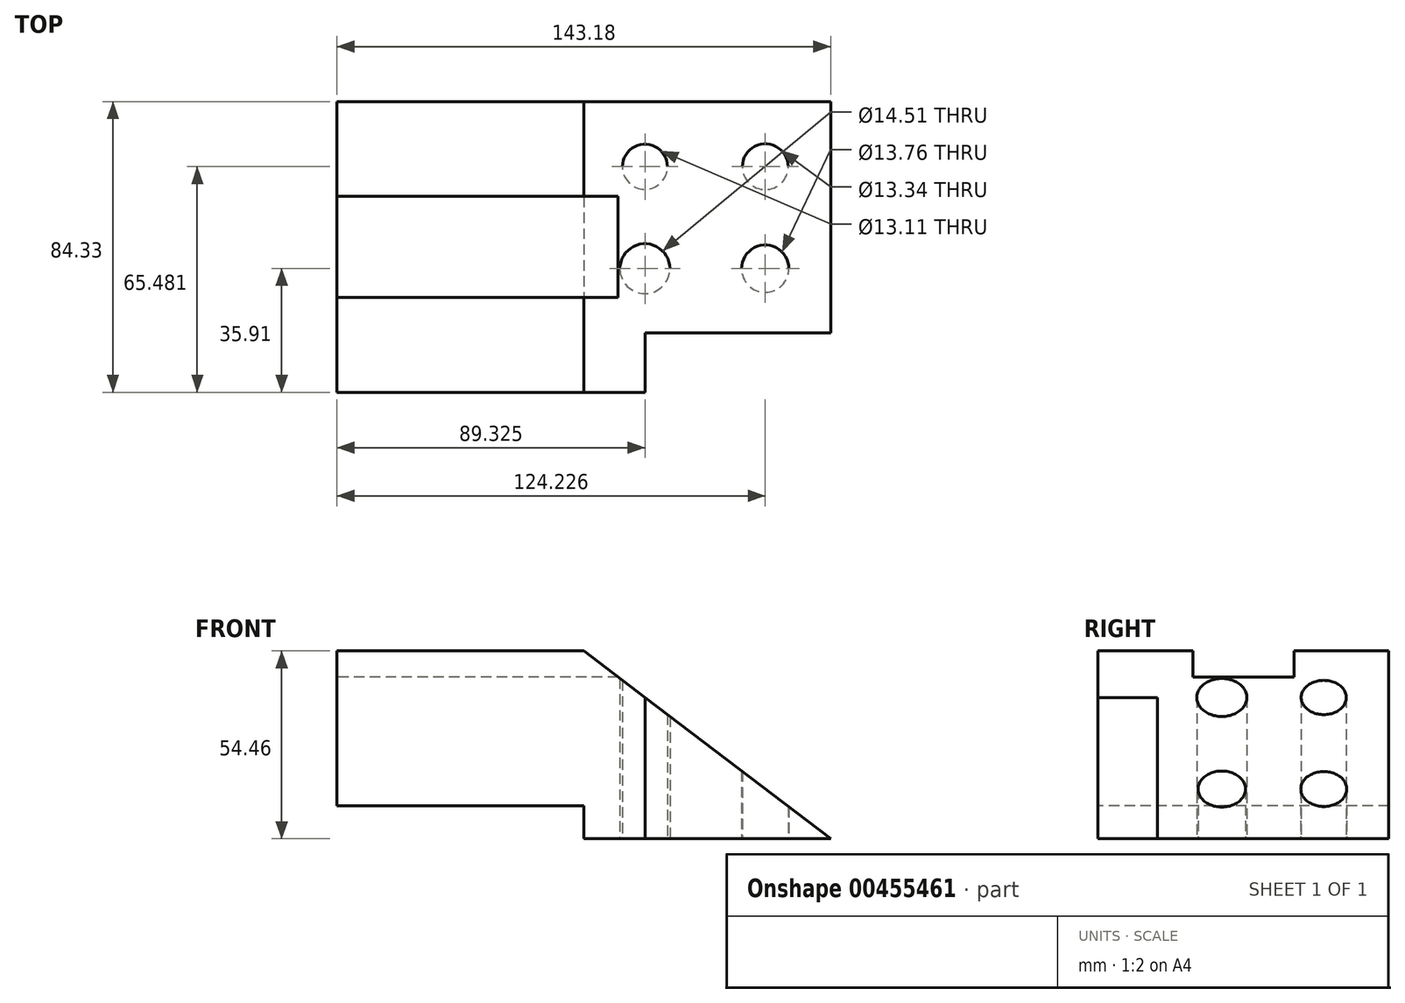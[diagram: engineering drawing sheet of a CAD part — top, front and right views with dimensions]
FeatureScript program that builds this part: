
annotation { "Feature Type Name" : "Feature", "Feature Type Description" : "" }
export const myFeature = defineFeature(function(context is Context, id is Id, definition is map)
    precondition{}
    {
        {
            var Q0;
            Q0=qCreatedBy(makeId("Front.planeOp"),FACE);
            var sketch = newSketch(context, id + "F0", { "sketchPlane" : qUnion([Q0])});
            skLineSegment(sketch, "E0.bottom", {"start": v(0, 27.23) * mm, "end": v(-71.59, 27.23) * mm});
            skLineSegment(sketch, "E0.top", {"start": v(71.59, -27.23) * mm, "end": v(-71.59, -27.23) * mm});
            skLineSegment(sketch, "E0.right", {"start": v(-71.59, 27.23) * mm, "end": v(-71.59, -27.23) * mm});
            skPoint(sketch, "E0.middle", {"position": v(0, 0) * mm});
            skLineSegment(sketch, "E1", {"start": v(0, 27.23) * mm, "end": v(71.59, -27.23) * mm});
            skSolve(sketch);
        }
        {
            var Q0;
            Q0=makeQuery(id+"F0.imprint","IMPRINT",FACE,{"disambiguationData":[TD([[makeQuery(id+"F0.imprint","IMPRINT",EDGE,{"derivedFrom":sQuery(id+"F0.wireOp",EDGE,"E0.bottom")}),1.0]])]});
            extrude(context, id + "F1", {"entities" : qUnion([Q0]), "depth" : 67.06 * mm});
        }
        {
            var Q0;
            Q0=makeQuery(id+"F1.opExtrude","CAP_FACE",FACE,{"disambiguationData":[OSD([sQuery(id+"F0.wireOp",EDGE,"E0.bottom"),sQuery(id+"F0.wireOp",EDGE,"E0.top"),sQuery(id+"F0.wireOp",EDGE,"E0.right"),sQuery(id+"F0.wireOp",EDGE,"E1")])],"isStart":false});
            var sketch = newSketch(context, id + "F2", { "sketchPlane" : qUnion([Q0])});
            skLineSegment(sketch, "E2", {"start": v(17.73, 13.74) * mm, "end": v(17.73, -27.23) * mm});
            skLineSegment(sketch, "E3", {"start": v(0, -27.23) * mm, "end": v(0, -22.04) * mm});
            skPoint(sketch, "E3.endSnap0", {"position": v(0, -27.23) * mm});
            skLineSegment(sketch, "E4", {"start": v(0, -22.04) * mm, "end": v(-71.59, -22.04) * mm});
            skSolve(sketch);
        }
        {
            var Q0;
            {var subQ0=sQuery(id+"F2.wireOp",EDGE,"E3");Q0=makeQuery(id+"F2.imprint","IMPRINT",FACE,{"disambiguationData":[TD([[makeQuery(id+"F2.imprint","IMPRINT",EDGE,{"derivedFrom":subQ0}),1.0]])]});}
            extrude(context, id + "F3", {"entities" : qUnion([Q0]), "operationType" : NewBodyOperationType.REMOVE, "oppositeDirection" : true, "depth" : 186.44 * mm});
        }
        {
            var Q0;
            {var subQ3=sQuery(id+"F2.wireOp",EDGE,"E2");Q0=makeQuery(id+"F2.imprint","IMPRINT",FACE,{"disambiguationData":[TD([[makeQuery(id+"F2.imprint","IMPRINT",EDGE,{"derivedFrom":subQ3}),-1.0]])]});}
            extrude(context, id + "F4", {"entities" : qUnion([Q0]), "operationType" : NewBodyOperationType.ADD, "depth" : 17.27 * mm});
        }
        {
            var Q0;
            {var subQ0=sQuery(id+"F2.wireOp",EDGE,"E4");Q0=makeQuery(id+"F4.boolean.opBoolean","MERGE",FACE,{"derivedFrom":[makeQuery(id+"F3.boolean.opBoolean","COPY",FACE,{"derivedFrom":makeQuery(id+"F3.opExtrude","SWEPT_FACE",FACE,{"disambiguationData":[OSD([subQ0])]})}),makeQuery(id+"F4.opExtrude","SWEPT_FACE",FACE,{"disambiguationData":[OSD([subQ0])]})]});}
            extrude(context, id + "F5", {"entities" : qUnion([Q0]), "operationType" : NewBodyOperationType.REMOVE, "oppositeDirection" : true, "depth" : 4.32 * mm});
        }
        {
            var Q0;
            {var subQ0=sQuery(id+"F0.wireOp",EDGE,"E0.right");Q0=makeQuery(id+"F4.boolean.opBoolean","MERGE",FACE,{"derivedFrom":[makeQuery(id+"F1.opExtrude","SWEPT_FACE",FACE,{"disambiguationData":[OSD([subQ0])]}),makeQuery(id+"F4.opExtrude","SWEPT_FACE",FACE,{"disambiguationData":[OSD([subQ0])]})]});}
            var sketch = newSketch(context, id + "F6", { "sketchPlane" : qUnion([Q0])});
            skLineSegment(sketch, "E5.bottom", {"start": v(56.82, 19.65) * mm, "end": v(27.51, 19.65) * mm});
            skLineSegment(sketch, "E5.top", {"start": v(56.82, 34.81) * mm, "end": v(27.51, 34.81) * mm});
            skLineSegment(sketch, "E5.left", {"start": v(56.82, 19.65) * mm, "end": v(56.82, 34.81) * mm});
            skLineSegment(sketch, "E5.right", {"start": v(27.51, 19.65) * mm, "end": v(27.51, 34.81) * mm});
            skPoint(sketch, "E5.middle", {"position": v(42.16, 27.23) * mm});
            skSolve(sketch);
        }
        {
            var Q0;
            {var subQ0=sQuery(id+"F6.wireOp",EDGE,"E5.bottom");Q0=makeQuery(id+"F6.imprint","IMPRINT",FACE,{"disambiguationData":[TD([[makeQuery(id+"F6.imprint","IMPRINT",EDGE,{"derivedFrom":subQ0}),-1.0]])]});}
            extrude(context, id + "F7", {"entities" : qUnion([Q0]), "operationType" : NewBodyOperationType.REMOVE, "oppositeDirection" : true, "depth" : 176.78 * mm});
        }
        {
            var Q0;
            {var subQ0=sQuery(id+"F0.wireOp",EDGE,"E0.top");Q0=makeQuery(id+"F4.boolean.opBoolean","MERGE",FACE,{"derivedFrom":[makeQuery(id+"F1.opExtrude","SWEPT_FACE",FACE,{"disambiguationData":[OSD([subQ0])]}),makeQuery(id+"F4.opExtrude","SWEPT_FACE",FACE,{"disambiguationData":[OSD([subQ0])]})]});}
            var sketch = newSketch(context, id + "F8", { "sketchPlane" : qUnion([Q0])});
            skCircle(sketch, "E6", {"center": v(52.64, 48.42) * mm, "radius": 6.88 * mm});
            skCircle(sketch, "E7", {"center": v(52.64, 18.85) * mm, "radius": 6.67 * mm});
            skCircle(sketch, "E8", {"center": v(17.73, 18.85) * mm, "radius": 6.55 * mm});
            skCircle(sketch, "E9", {"center": v(17.73, 48.42) * mm, "radius": 7.26 * mm});
            skSolve(sketch);
        }
        {
            var Q0;
            Q0=makeQuery(id+"F8.imprint","IMPRINT",FACE,{"disambiguationData":[TD([[makeQuery(id+"F8.imprint","IMPRINT",EDGE,{"derivedFrom":sQuery(id+"F8.wireOp",EDGE,"E9")}),1.0]])]});
            var Q1;
            Q1=makeQuery(id+"F8.imprint","IMPRINT",FACE,{"disambiguationData":[TD([[makeQuery(id+"F8.imprint","IMPRINT",EDGE,{"derivedFrom":sQuery(id+"F8.wireOp",EDGE,"E6")}),1.0]])]});
            var Q2;
            Q2=makeQuery(id+"F8.imprint","IMPRINT",FACE,{"disambiguationData":[TD([[makeQuery(id+"F8.imprint","IMPRINT",EDGE,{"derivedFrom":sQuery(id+"F8.wireOp",EDGE,"E7")}),1.0]])]});
            var Q3;
            Q3=makeQuery(id+"F8.imprint","IMPRINT",FACE,{"disambiguationData":[TD([[makeQuery(id+"F8.imprint","IMPRINT",EDGE,{"derivedFrom":sQuery(id+"F8.wireOp",EDGE,"E8")}),1.0]])]});
            extrude(context, id + "F9", {"entities" : qUnion([Q0, Q1, Q2, Q3]), "operationType" : NewBodyOperationType.REMOVE, "oppositeDirection" : true, "depth" : 94.74 * mm});
        }
    });
